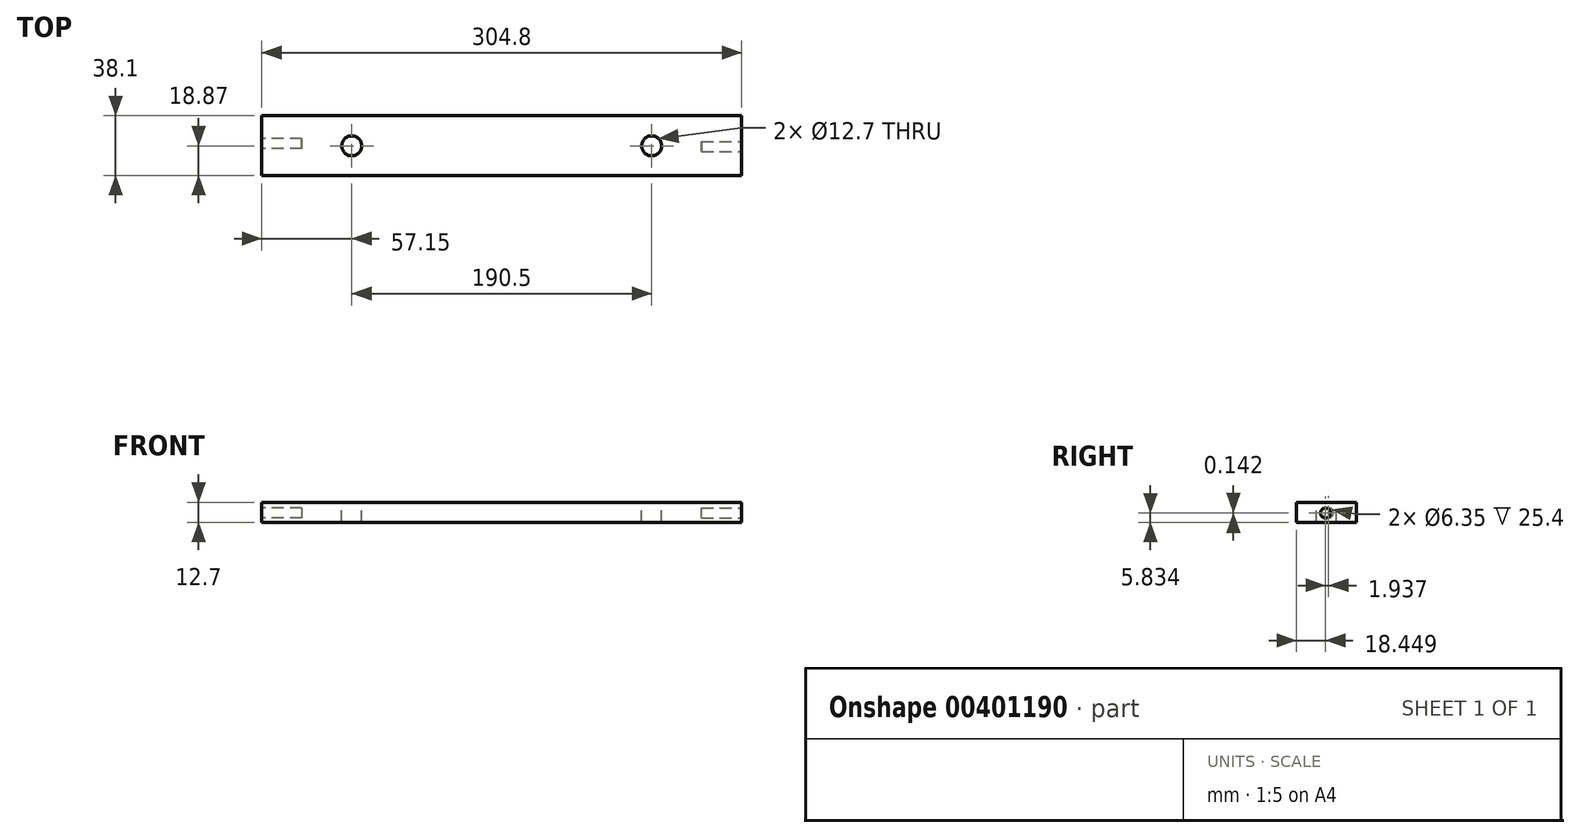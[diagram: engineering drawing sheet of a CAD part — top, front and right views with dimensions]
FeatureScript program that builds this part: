
annotation { "Feature Type Name" : "Feature", "Feature Type Description" : "" }
export const myFeature = defineFeature(function(context is Context, id is Id, definition is map)
    precondition{}
    {
        {
            var Q0;
            Q0=qCreatedBy(makeId("Top.planeOp"),FACE);
            var sketch = newSketch(context, id + "F0", { "sketchPlane" : qUnion([Q0])});
            skLineSegment(sketch, "E0.bottom", {"start": v(0, 0) * mm, "end": v(-304.8, 0) * mm});
            skLineSegment(sketch, "E0.top", {"start": v(0, 38.1) * mm, "end": v(-304.8, 38.1) * mm});
            skLineSegment(sketch, "E0.left", {"start": v(0, 0) * mm, "end": v(0, 38.1) * mm});
            skLineSegment(sketch, "E0.right", {"start": v(-304.8, 0) * mm, "end": v(-304.8, 38.1) * mm});
            skSolve(sketch);
        }
        {
            var Q0;
            Q0 = qSketchRegion(id + "F0", true);
            extrude(context, id + "F1", {"entities" : qUnion([Q0]), "depth" : 12.7 * mm});
        }
        {
            var Q0;
            Q0=makeQuery(id+"F1.opExtrude","SWEPT_FACE",FACE,{"disambiguationData":[OSD([sQuery(id+"F0.wireOp",EDGE,"E0.left")])]});
            var sketch = newSketch(context, id + "F2", { "sketchPlane" : qUnion([Q0])});
            skCircle(sketch, "E1", {"center": v(18.45, 5.83) * mm, "radius": 3.18 * mm});
            skSolve(sketch);
        }
        {
            var Q0;
            Q0 = qSketchRegion(id + "F2", true);
            extrude(context, id + "F3", {"entities" : qUnion([Q0]), "operationType" : NewBodyOperationType.REMOVE, "oppositeDirection" : true, "depth" : 25.4 * mm});
        }
        {
            var Q0;
            Q0=makeQuery(id+"F1.opExtrude","SWEPT_FACE",FACE,{"disambiguationData":[OSD([sQuery(id+"F0.wireOp",EDGE,"E0.right")])]});
            var sketch = newSketch(context, id + "F4", { "sketchPlane" : qUnion([Q0])});
            skCircle(sketch, "E2", {"center": v(-20.39, 5.98) * mm, "radius": 3.18 * mm});
            skSolve(sketch);
        }
        {
            var Q0;
            Q0 = qSketchRegion(id + "F4", true);
            extrude(context, id + "F5", {"entities" : qUnion([Q0]), "operationType" : NewBodyOperationType.REMOVE, "oppositeDirection" : true, "depth" : 25.4 * mm});
        }
        {
            var Q0;
            Q0=makeQuery(id+"F1.opExtrude","CAP_FACE",FACE,{"disambiguationData":[OSD([sQuery(id+"F0.wireOp",EDGE,"E0.bottom"),sQuery(id+"F0.wireOp",EDGE,"E0.top"),sQuery(id+"F0.wireOp",EDGE,"E0.left"),sQuery(id+"F0.wireOp",EDGE,"E0.right")])],"isStart":false});
            var sketch = newSketch(context, id + "F6", { "sketchPlane" : qUnion([Q0])});
            skCircle(sketch, "E3", {"center": v(-247.65, 18.87) * mm, "radius": 6.35 * mm});
            skCircle(sketch, "E4", {"center": v(-57.15, 18.87) * mm, "radius": 6.35 * mm});
            skSolve(sketch);
        }
        {
            var Q0;
            Q0 = qSketchRegion(id + "F6", true);
            extrude(context, id + "F7", {"entities" : qUnion([Q0]), "operationType" : NewBodyOperationType.REMOVE, "endBound" : BoundingType.THROUGH_ALL, "oppositeDirection" : true, "depth" : 25.4 * mm});
        }
    });
